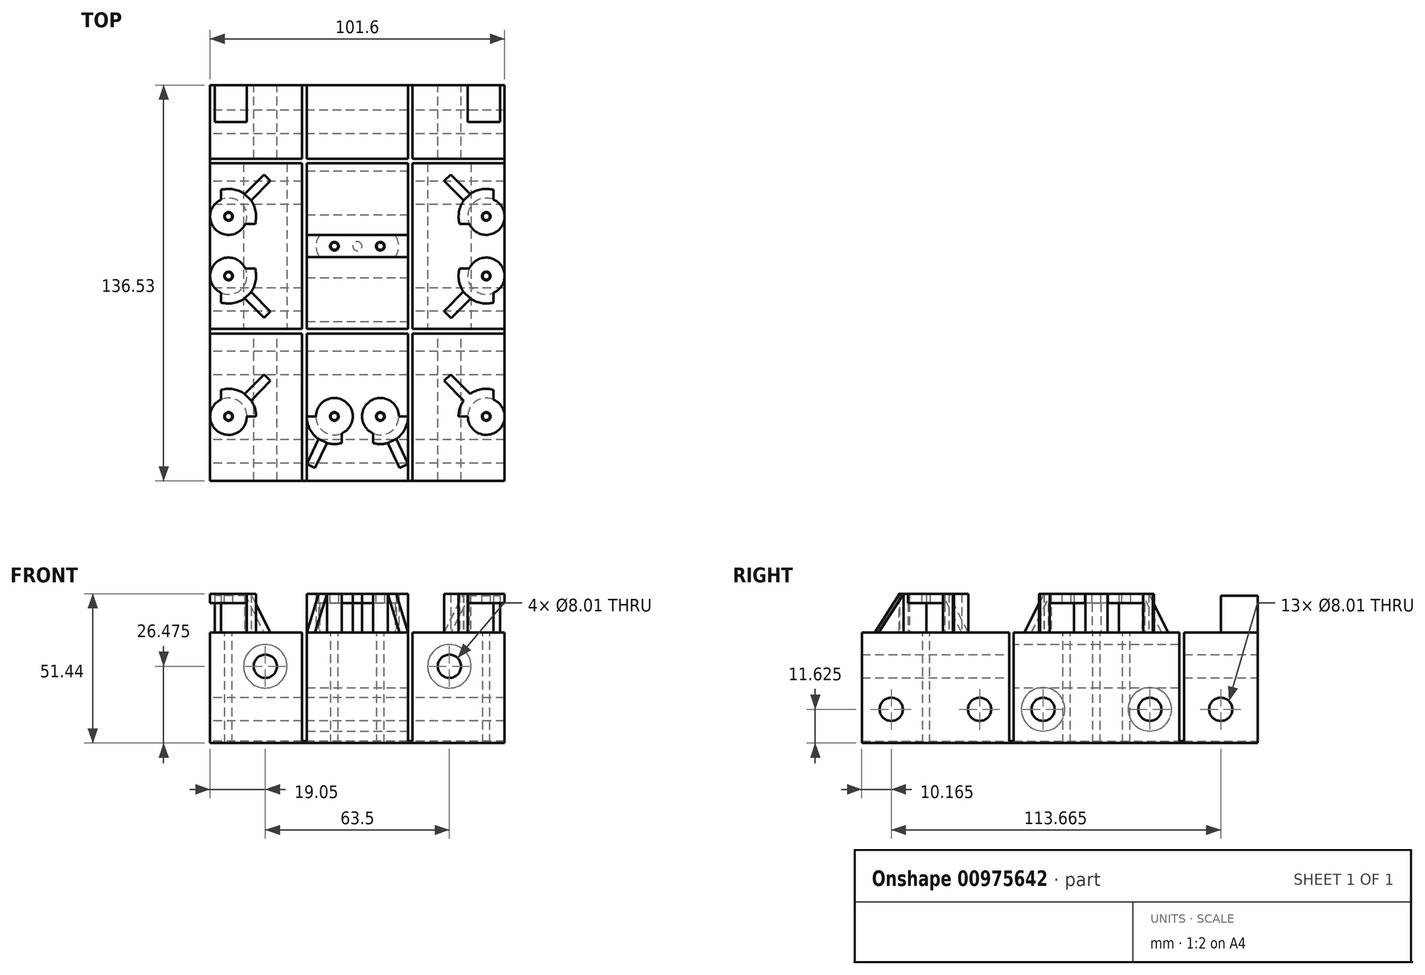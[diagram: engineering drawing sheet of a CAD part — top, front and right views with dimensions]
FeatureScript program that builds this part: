
annotation { "Feature Type Name" : "Feature", "Feature Type Description" : "" }
export const myFeature = defineFeature(function(context is Context, id is Id, definition is map)
    precondition{}
    {
        {
            var Q0;
            Q0=qCreatedBy(makeId("Front.planeOp"),FACE);
            var sketch = newSketch(context, id + "F0", { "sketchPlane" : qUnion([Q0])});
            skLineSegment(sketch, "E0.bottom", {"start": v(-50.8, 0) * mm, "end": v(50.8, 0) * mm});
            skLineSegment(sketch, "E0.top", {"start": v(-50.8, 38.1) * mm, "end": v(-19.05, 38.1) * mm});
            skLineSegment(sketch, "E0.left", {"start": v(-50.8, 0) * mm, "end": v(-50.8, 38.1) * mm});
            skLineSegment(sketch, "E0.right", {"start": v(50.8, 0) * mm, "end": v(50.8, 38.1) * mm});
            skLineSegment(sketch, "E1", {"start": v(-19.05, 38.1) * mm, "end": v(-19.05, 0.64) * mm});
            skLineSegment(sketch, "E2", {"start": v(-19.05, 0.64) * mm, "end": v(-17.46, 0.64) * mm});
            skLineSegment(sketch, "E3", {"start": v(-17.46, 0.64) * mm, "end": v(-17.46, 38.1) * mm});
            skLineSegment(sketch, "E4", {"start": v(17.46, 38.1) * mm, "end": v(17.46, 0.64) * mm});
            skLineSegment(sketch, "E5", {"start": v(17.46, 0.64) * mm, "end": v(19.05, 0.64) * mm});
            skLineSegment(sketch, "E6", {"start": v(19.05, 0.64) * mm, "end": v(19.05, 38.1) * mm});
            skLineSegment(sketch, "E7.trimOffspring", {"start": v(-17.46, 38.1) * mm, "end": v(17.46, 38.1) * mm});
            skLineSegment(sketch, "E8.trimOffspring", {"start": v(19.05, 38.1) * mm, "end": v(50.8, 38.1) * mm});
            skLineSegment(sketch, "E9", {"start": v(-50.8, 26.47) * mm, "end": v(50.8, 26.48) * mm, "construction": true});
            skCircle(sketch, "E10", {"center": v(-31.75, 26.47) * mm, "radius": 4 * mm});
            skCircle(sketch, "E11", {"center": v(31.75, 26.48) * mm, "radius": 4 * mm});
            skLineSegment(sketch, "E12", {"start": v(31.75, 38.1) * mm, "end": v(31.75, 0) * mm, "construction": true});
            skLineSegment(sketch, "E13", {"start": v(-31.75, 38.1) * mm, "end": v(-31.75, 0) * mm, "construction": true});
            skSolve(sketch);
        }
        {
            var Q0;
            Q0 = qSketchRegion(id + "F0", true);
            extrude(context, id + "F1", {"entities" : qUnion([Q0]), "depth" : 136.53 * mm, "offsetDistance" : 25.4 * mm});
        }
        {
            var Q0;
            Q0=makeQuery(id+"F1.opExtrude","SWEPT_FACE",FACE,{"disambiguationData":[OSD([sQuery(id+"F0.wireOp",EDGE,"E0.left")])]});
            var sketch = newSketch(context, id + "F2", { "sketchPlane" : qUnion([Q0])});
            skLineSegment(sketch, "E14.bottom", {"start": v(25.4, 64.27) * mm, "end": v(26.99, 64.27) * mm});
            skLineSegment(sketch, "E14.top", {"start": v(25.4, 0.64) * mm, "end": v(26.99, 0.64) * mm});
            skLineSegment(sketch, "E14.left", {"start": v(25.4, 64.27) * mm, "end": v(25.4, 0.64) * mm});
            skLineSegment(sketch, "E14.right", {"start": v(26.99, 64.27) * mm, "end": v(26.99, 0.64) * mm});
            skLineSegment(sketch, "E15.bottom", {"start": v(84.14, 64.27) * mm, "end": v(85.72, 64.27) * mm});
            skLineSegment(sketch, "E15.top", {"start": v(84.14, 0.64) * mm, "end": v(85.72, 0.64) * mm});
            skLineSegment(sketch, "E15.left", {"start": v(84.14, 64.27) * mm, "end": v(84.14, 0.64) * mm});
            skLineSegment(sketch, "E15.right", {"start": v(85.72, 64.27) * mm, "end": v(85.72, 0.64) * mm});
            skCircle(sketch, "E16", {"center": v(12.7, 11.63) * mm, "radius": 4 * mm});
            skCircle(sketch, "E17", {"center": v(37.15, 11.63) * mm, "radius": 4 * mm});
            skCircle(sketch, "E18", {"center": v(73.98, 11.63) * mm, "radius": 4 * mm});
            skCircle(sketch, "E19", {"center": v(95.88, 11.63) * mm, "radius": 4 * mm});
            skCircle(sketch, "E20", {"center": v(126.37, 11.63) * mm, "radius": 4 * mm});
            skLineSegment(sketch, "E21", {"start": v(0, 11.62) * mm, "end": v(175.3, 11.63) * mm, "construction": true});
            skSolve(sketch);
        }
        {
            var Q0;
            Q0 = qSketchRegion(id + "F2", true);
            extrude(context, id + "F3", {"entities" : qUnion([Q0]), "operationType" : NewBodyOperationType.REMOVE, "endBound" : BoundingType.THROUGH_ALL, "oppositeDirection" : true, "depth" : 25.4 * mm, "offsetDistance" : 25.4 * mm});
        }
        {
            var Q0;
            Q0=makeQuery(id+"F3.boolean.opBoolean","COPY",FACE,{"disambiguationData":[TD([makeQuery(id+"F1.opExtrude","SWEPT_FACE",FACE,{"disambiguationData":[OSD([sQuery(id+"F0.wireOp",EDGE,"E0.right")])]})])],"derivedFrom":makeQuery(id+"F3.opExtrude","SWEPT_FACE",FACE,{"disambiguationData":[OSD([sQuery(id+"F2.wireOp",EDGE,"E15.left")])]})});
            var sketch = newSketch(context, id + "F4", { "sketchPlane" : qUnion([Q0])});
            skCircle(sketch, "E22", {"center": v(31.75, 26.48) * mm, "radius": 7.5 * mm});
            skCircle(sketch, "E23.0", {"center": v(-31.75, 26.47) * mm, "radius": 4 * mm, "construction": true});
            skCircle(sketch, "E24", {"center": v(-31.75, 26.47) * mm, "radius": 7.5 * mm});
            skSolve(sketch);
        }
        {
            var Q0;
            Q0 = qSketchRegion(id + "F4", true);
            var Q1;
            Q1=makeQuery(id+"F3.boolean.opBoolean","COPY",FACE,{"disambiguationData":[TD([makeQuery(id+"F1.opExtrude","SWEPT_FACE",FACE,{"disambiguationData":[OSD([sQuery(id+"F0.wireOp",EDGE,"E0.right")])]})])],"derivedFrom":makeQuery(id+"F3.opExtrude","SWEPT_FACE",FACE,{"disambiguationData":[OSD([sQuery(id+"F2.wireOp",EDGE,"E14.left")])]})});
            extrude(context, id + "F5", {"entities" : qUnion([Q0]), "operationType" : NewBodyOperationType.REMOVE, "endBound" : BoundingType.UP_TO_SURFACE, "oppositeDirection" : true, "depth" : 25.4 * mm, "endBoundEntityFace" : qUnion([Q1]), "offsetDistance" : 25.4 * mm});
        }
        {
            var Q0;
            Q0=makeQuery(id+"F3.boolean.opBoolean","SPLIT",FACE,{"disambiguationData":[TD([makeQuery(id+"F3.opExtrude","SWEPT_FACE",FACE,{"disambiguationData":[OSD([sQuery(id+"F2.wireOp",EDGE,"E14.right")])]})])],"derivedFrom":makeQuery(id+"F1.opExtrude","SWEPT_FACE",FACE,{"disambiguationData":[OSD([sQuery(id+"F0.wireOp",EDGE,"E4")])]})});
            var sketch = newSketch(context, id + "F6", { "sketchPlane" : qUnion([Q0])});
            skCircle(sketch, "E25", {"center": v(-73.98, 11.63) * mm, "radius": 7.5 * mm});
            skCircle(sketch, "E26", {"center": v(-37.15, 11.63) * mm, "radius": 7.5 * mm});
            skSolve(sketch);
        }
        {
            var Q0;
            Q0 = qSketchRegion(id + "F6", true);
            var Q1;
            Q1=makeQuery(id+"F3.boolean.opBoolean","SPLIT",FACE,{"disambiguationData":[TD([makeQuery(id+"F3.opExtrude","SWEPT_FACE",FACE,{"disambiguationData":[OSD([sQuery(id+"F2.wireOp",EDGE,"E14.right")])]})])],"derivedFrom":makeQuery(id+"F1.opExtrude","SWEPT_FACE",FACE,{"disambiguationData":[OSD([sQuery(id+"F0.wireOp",EDGE,"E1")])]})});
            extrude(context, id + "F7", {"entities" : qUnion([Q0]), "operationType" : NewBodyOperationType.REMOVE, "endBound" : BoundingType.UP_TO_SURFACE, "oppositeDirection" : true, "depth" : 25.4 * mm, "endBoundEntityFace" : qUnion([Q1]), "offsetDistance" : 25.4 * mm});
        }
        {
            var Q0;
            {var subQ0=sQuery(id+"F0.wireOp",EDGE,"E8.trimOffspring");Q0=makeQuery(id+"F3.boolean.opBoolean","SPLIT",FACE,{"disambiguationData":[TD([makeQuery(id+"F3.opExtrude","SWEPT_FACE",FACE,{"disambiguationData":[OSD([sQuery(id+"F2.wireOp",EDGE,"E15.right")])]})])],"derivedFrom":makeQuery(id+"F1.opExtrude","SWEPT_FACE",FACE,{"disambiguationData":[OSD([subQ0])]})});}
            var sketch = newSketch(context, id + "F8", { "sketchPlane" : qUnion([Q0])});
            skLineSegment(sketch, "E27.0.0", {"start": v(19.05, -84.14) * mm, "end": v(50.8, -84.14) * mm, "construction": true});
            skLineSegment(sketch, "E27.0.1", {"start": v(50.8, -84.14) * mm, "end": v(50.8, -26.99) * mm, "construction": true});
            skLineSegment(sketch, "E27.0.2", {"start": v(50.8, -26.99) * mm, "end": v(19.05, -26.99) * mm, "construction": true});
            skLineSegment(sketch, "E27.0.3", {"start": v(19.05, -26.99) * mm, "end": v(19.05, -84.14) * mm, "construction": true});
            skLineSegment(sketch, "E28.0.0", {"start": v(17.46, -136.53) * mm, "end": v(17.46, -85.72) * mm, "construction": true});
            skLineSegment(sketch, "E28.0.1", {"start": v(17.46, -85.72) * mm, "end": v(-17.46, -85.72) * mm, "construction": true});
            skLineSegment(sketch, "E28.0.2", {"start": v(-17.46, -85.72) * mm, "end": v(-17.46, -136.53) * mm, "construction": true});
            skLineSegment(sketch, "E28.0.3", {"start": v(-17.46, -136.53) * mm, "end": v(17.46, -136.53) * mm, "construction": true});
            skLineSegment(sketch, "E29.0.0", {"start": v(-17.46, -84.14) * mm, "end": v(17.46, -84.14) * mm, "construction": true});
            skLineSegment(sketch, "E29.0.1", {"start": v(17.46, -84.14) * mm, "end": v(17.46, -26.99) * mm, "construction": true});
            skLineSegment(sketch, "E29.0.2", {"start": v(17.46, -26.99) * mm, "end": v(-17.46, -26.99) * mm, "construction": true});
            skLineSegment(sketch, "E29.0.3", {"start": v(-17.46, -26.99) * mm, "end": v(-17.46, -84.14) * mm, "construction": true});
            skLineSegment(sketch, "E30.0.0", {"start": v(-19.05, -136.53) * mm, "end": v(-19.05, -85.72) * mm, "construction": true});
            skLineSegment(sketch, "E30.0.1", {"start": v(-19.05, -85.72) * mm, "end": v(-50.8, -85.72) * mm, "construction": true});
            skLineSegment(sketch, "E30.0.2", {"start": v(-50.8, -85.72) * mm, "end": v(-50.8, -136.53) * mm, "construction": true});
            skLineSegment(sketch, "E30.0.3", {"start": v(-50.8, -136.53) * mm, "end": v(-19.05, -136.53) * mm, "construction": true});
            skLineSegment(sketch, "E31.0.0", {"start": v(-50.8, -84.14) * mm, "end": v(-19.05, -84.14) * mm, "construction": true});
            skLineSegment(sketch, "E31.0.1", {"start": v(-19.05, -84.14) * mm, "end": v(-19.05, -26.99) * mm, "construction": true});
            skLineSegment(sketch, "E31.0.2", {"start": v(-19.05, -26.99) * mm, "end": v(-50.8, -26.99) * mm, "construction": true});
            skLineSegment(sketch, "E31.0.3", {"start": v(-50.8, -26.99) * mm, "end": v(-50.8, -84.14) * mm, "construction": true});
            skLineSegment(sketch, "E32.0.0", {"start": v(-17.46, -25.4) * mm, "end": v(17.46, -25.4) * mm, "construction": true});
            skLineSegment(sketch, "E32.0.1", {"start": v(17.46, -25.4) * mm, "end": v(17.46, 0) * mm, "construction": true});
            skLineSegment(sketch, "E32.0.2", {"start": v(17.46, 0) * mm, "end": v(-17.46, 0) * mm, "construction": true});
            skLineSegment(sketch, "E32.0.3", {"start": v(-17.46, 0) * mm, "end": v(-17.46, -25.4) * mm, "construction": true});
            skLineSegment(sketch, "E33.0.0", {"start": v(19.05, -25.4) * mm, "end": v(50.8, -25.4) * mm, "construction": true});
            skLineSegment(sketch, "E33.0.1", {"start": v(50.8, -25.4) * mm, "end": v(50.8, 0) * mm, "construction": true});
            skLineSegment(sketch, "E33.0.2", {"start": v(50.8, 0) * mm, "end": v(19.05, 0) * mm, "construction": true});
            skLineSegment(sketch, "E33.0.3", {"start": v(19.05, 0) * mm, "end": v(19.05, -25.4) * mm, "construction": true});
            skLineSegment(sketch, "E34.0.0", {"start": v(-50.8, -25.4) * mm, "end": v(-19.05, -25.4) * mm, "construction": true});
            skLineSegment(sketch, "E34.0.1", {"start": v(-19.05, -25.4) * mm, "end": v(-19.05, 0) * mm, "construction": true});
            skLineSegment(sketch, "E34.0.2", {"start": v(-19.05, 0) * mm, "end": v(-50.8, 0) * mm, "construction": true});
            skLineSegment(sketch, "E34.0.3", {"start": v(-50.8, 0) * mm, "end": v(-50.8, -25.4) * mm, "construction": true});
            skLineSegment(sketch, "E35.0", {"start": v(50.8, -85.72) * mm, "end": v(19.05, -85.72) * mm, "construction": true});
            skLineSegment(sketch, "E36.0", {"start": v(19.05, -136.53) * mm, "end": v(19.05, -85.72) * mm, "construction": true});
            skLineSegment(sketch, "E37.0", {"start": v(19.05, -136.53) * mm, "end": v(50.8, -136.53) * mm, "construction": true});
            skLineSegment(sketch, "E38.0", {"start": v(50.8, -136.53) * mm, "end": v(50.8, -85.72) * mm, "construction": true});
            skLineSegment(sketch, "E39", {"start": v(44.45, 0) * mm, "end": v(44.45, -136.53) * mm, "construction": true});
            skPoint(sketch, "E40.endSnap0", {"position": v(0, -84.14) * mm});
            skLineSegment(sketch, "E41", {"start": v(-44.45, 0) * mm, "end": v(-44.45, -136.53) * mm, "construction": true});
            skLineSegment(sketch, "E42", {"start": v(-50.8, -114.3) * mm, "end": v(50.8, -114.3) * mm, "construction": true});
            skLineSegment(sketch, "E43", {"start": v(-50.8, -55.56) * mm, "end": v(50.8, -55.56) * mm, "construction": true});
            skLineSegment(sketch, "E44", {"start": v(50.8, -65.82) * mm, "end": v(-50.8, -65.82) * mm, "construction": true});
            skLineSegment(sketch, "E45", {"start": v(50.8, -45.3) * mm, "end": v(-50.8, -45.3) * mm, "construction": true});
            skCircle(sketch, "E46", {"center": v(7.92, -55.56) * mm, "radius": 4.75 * mm, "construction": true});
            skCircle(sketch, "E47", {"center": v(44.45, -45.3) * mm, "radius": 4.75 * mm, "construction": true});
            skCircle(sketch, "E48", {"center": v(44.45, -65.82) * mm, "radius": 4.75 * mm, "construction": true});
            skCircle(sketch, "E49", {"center": v(-44.45, -45.3) * mm, "radius": 4.75 * mm, "construction": true});
            skCircle(sketch, "E50", {"center": v(-44.45, -65.82) * mm, "radius": 4.75 * mm, "construction": true});
            skCircle(sketch, "E51", {"center": v(44.45, -114.3) * mm, "radius": 4.75 * mm, "construction": true});
            skCircle(sketch, "E52", {"center": v(-44.45, -114.3) * mm, "radius": 4.75 * mm, "construction": true});
            skCircle(sketch, "E53", {"center": v(0, -55.56) * mm, "radius": 3.18 * mm, "construction": true});
            skLineSegment(sketch, "E54", {"start": v(-50.8, -61.07) * mm, "end": v(50.8, -61.07) * mm, "construction": true});
            skLineSegment(sketch, "E55", {"start": v(50.8, -50.05) * mm, "end": v(-50.8, -50.05) * mm, "construction": true});
            skLineSegment(sketch, "E56", {"start": v(-50.8, -60.31) * mm, "end": v(50.8, -60.31) * mm, "construction": true});
            skLineSegment(sketch, "E57", {"start": v(-50.8, -50.81) * mm, "end": v(50.8, -50.81) * mm, "construction": true});
            skCircle(sketch, "E58", {"center": v(-7.92, -55.56) * mm, "radius": 4.75 * mm, "construction": true});
            skCircle(sketch, "E59", {"center": v(-44.45, -45.3) * mm, "radius": 1.25 * mm});
            skCircle(sketch, "E60", {"center": v(44.45, -45.3) * mm, "radius": 1.25 * mm});
            skCircle(sketch, "E61", {"center": v(7.92, -55.56) * mm, "radius": 1.25 * mm});
            skCircle(sketch, "E62", {"center": v(-7.92, -55.56) * mm, "radius": 1.25 * mm});
            skCircle(sketch, "E63", {"center": v(-44.45, -65.82) * mm, "radius": 1.25 * mm});
            skCircle(sketch, "E64", {"center": v(-44.45, -114.3) * mm, "radius": 1.25 * mm});
            skCircle(sketch, "E65", {"center": v(44.45, -65.82) * mm, "radius": 1.25 * mm});
            skCircle(sketch, "E66", {"center": v(44.45, -114.3) * mm, "radius": 1.25 * mm});
            skCircle(sketch, "E67", {"center": v(7.94, -114.3) * mm, "radius": 1.25 * mm});
            skCircle(sketch, "E68", {"center": v(-7.94, -114.3) * mm, "radius": 1.25 * mm});
            skCircle(sketch, "E69", {"center": v(7.94, -114.3) * mm, "radius": 4.75 * mm, "construction": true});
            skCircle(sketch, "E70", {"center": v(-7.94, -114.3) * mm, "radius": 4.75 * mm, "construction": true});
            skSolve(sketch);
        }
        {
            var Q0;
            Q0 = qSketchRegion(id + "F8", true);
            extrude(context, id + "F9", {"entities" : qUnion([Q0]), "operationType" : NewBodyOperationType.REMOVE, "endBound" : BoundingType.THROUGH_ALL, "oppositeDirection" : true, "depth" : 25.4 * mm, "offsetDistance" : 25.4 * mm});
        }
        {
            var Q0;
            {var subQ0=sQuery(id+"F0.wireOp",EDGE,"E8.trimOffspring");Q0=makeQuery(id+"F3.boolean.opBoolean","SPLIT",FACE,{"disambiguationData":[TD([makeQuery(id+"F3.opExtrude","SWEPT_FACE",FACE,{"disambiguationData":[OSD([sQuery(id+"F2.wireOp",EDGE,"E14.left")])]})])],"derivedFrom":makeQuery(id+"F1.opExtrude","SWEPT_FACE",FACE,{"disambiguationData":[OSD([subQ0])]})});}
            var sketch = newSketch(context, id + "F10", { "sketchPlane" : qUnion([Q0])});
            skCircle(sketch, "E71.0", {"center": v(44.45, -45.3) * mm, "radius": 4.75 * mm, "construction": true});
            skCircle(sketch, "E72.0", {"center": v(-44.45, -45.3) * mm, "radius": 4.75 * mm, "construction": true});
            skLineSegment(sketch, "E73.bottom", {"start": v(49.2, -12.7) * mm, "end": v(38.1, -12.7) * mm});
            skLineSegment(sketch, "E73.top", {"start": v(49.2, 0) * mm, "end": v(38.1, 0) * mm});
            skLineSegment(sketch, "E73.left", {"start": v(49.2, -12.7) * mm, "end": v(49.2, 0) * mm});
            skLineSegment(sketch, "E73.right", {"start": v(38.1, -12.7) * mm, "end": v(38.1, 0) * mm});
            skLineSegment(sketch, "E74.bottom", {"start": v(-38.1, 0) * mm, "end": v(-49.2, 0) * mm});
            skLineSegment(sketch, "E74.top", {"start": v(-38.1, -12.7) * mm, "end": v(-49.2, -12.7) * mm});
            skLineSegment(sketch, "E74.left", {"start": v(-38.1, 0) * mm, "end": v(-38.1, -12.7) * mm});
            skLineSegment(sketch, "E74.right", {"start": v(-49.2, 0) * mm, "end": v(-49.2, -12.7) * mm});
            skSolve(sketch);
        }
        {
            var Q0;
            Q0 = qSketchRegion(id + "F10", true);
            extrude(context, id + "F11", {"entities" : qUnion([Q0]), "operationType" : NewBodyOperationType.ADD, "depth" : 12.7 * mm, "offsetDistance" : 25.4 * mm});
        }
        {
            var Q0;
            {var subQ2=sQuery(id+"F0.wireOp",EDGE,"E0.top");Q0=makeQuery(id+"F3.boolean.opBoolean","SPLIT",FACE,{"disambiguationData":[TD([makeQuery(id+"F3.opExtrude","SWEPT_FACE",FACE,{"disambiguationData":[OSD([sQuery(id+"F2.wireOp",EDGE,"E15.right")])]})])],"derivedFrom":makeQuery(id+"F1.opExtrude","SWEPT_FACE",FACE,{"disambiguationData":[OSD([subQ2])]})});}
            var sketch = newSketch(context, id + "F12", { "sketchPlane" : qUnion([Q0])});
            skCircle(sketch, "E75.0", {"center": v(-44.45, -114.3) * mm, "radius": 4.75 * mm, "construction": true});
            skCircle(sketch, "E76.0", {"center": v(-7.94, -114.3) * mm, "radius": 4.75 * mm, "construction": true});
            skCircle(sketch, "E77.0", {"center": v(7.94, -114.3) * mm, "radius": 4.75 * mm, "construction": true});
            skCircle(sketch, "E78.0", {"center": v(-44.45, -65.82) * mm, "radius": 4.75 * mm, "construction": true});
            skCircle(sketch, "E79.0", {"center": v(44.45, -114.3) * mm, "radius": 4.75 * mm, "construction": true});
            skCircle(sketch, "E80.0", {"center": v(44.45, -65.82) * mm, "radius": 4.75 * mm, "construction": true});
            skCircle(sketch, "E81.0", {"center": v(44.45, -45.3) * mm, "radius": 4.75 * mm, "construction": true});
            skCircle(sketch, "E82.0", {"center": v(7.92, -55.56) * mm, "radius": 4.75 * mm, "construction": true});
            skCircle(sketch, "E83.0", {"center": v(-7.92, -55.56) * mm, "radius": 4.75 * mm, "construction": true});
            skCircle(sketch, "E84.0", {"center": v(-44.45, -45.3) * mm, "radius": 4.75 * mm, "construction": true});
            skArc(sketch, "E85", {"start": v(-38.1, -114.3) * mm, "mid": v(-40.97, -108.99) * mm, "end": v(-47, -108.48) * mm});
            skArc(sketch, "E86", {"start": v(-34.93, -114.3) * mm, "mid": v(-38.68, -106.72) * mm, "end": v(-47, -105.12) * mm});
            skLineSegment(sketch, "E87", {"start": v(38.1, -114.3) * mm, "end": v(34.92, -114.3) * mm});
            skLineSegment(sketch, "E88", {"start": v(-47, -36.12) * mm, "end": v(-47, -39.48) * mm});
            skArc(sketch, "E89", {"start": v(-47, -71.64) * mm, "mid": v(-39.96, -70.31) * mm, "end": v(-38.63, -63.28) * mm});
            skArc(sketch, "E90", {"start": v(-38.63, -47.84) * mm, "mid": v(-39.96, -40.81) * mm, "end": v(-47, -39.48) * mm});
            skArc(sketch, "E91", {"start": v(-35.27, -47.84) * mm, "mid": v(-37.71, -38.57) * mm, "end": v(-47, -36.12) * mm});
            skArc(sketch, "E92", {"start": v(-47, -75) * mm, "mid": v(-37.71, -72.56) * mm, "end": v(-35.27, -63.28) * mm});
            skArc(sketch, "E93", {"start": v(38.63, -63.28) * mm, "mid": v(39.96, -70.31) * mm, "end": v(46.99, -71.64) * mm});
            skArc(sketch, "E94", {"start": v(35.27, -63.28) * mm, "mid": v(37.71, -72.56) * mm, "end": v(47, -75) * mm});
            skArc(sketch, "E95", {"start": v(46.99, -39.48) * mm, "mid": v(39.96, -40.81) * mm, "end": v(38.63, -47.84) * mm});
            skArc(sketch, "E96", {"start": v(46.99, -36.12) * mm, "mid": v(37.71, -38.57) * mm, "end": v(35.27, -47.84) * mm});
            skArc(sketch, "E97", {"start": v(46.99, -108.48) * mm, "mid": v(40.97, -108.99) * mm, "end": v(38.1, -114.3) * mm});
            skArc(sketch, "E98", {"start": v(46.99, -105.12) * mm, "mid": v(38.68, -106.72) * mm, "end": v(34.92, -114.3) * mm});
            skLineSegment(sketch, "E99", {"start": v(46.99, -108.48) * mm, "end": v(46.99, -105.12) * mm});
            skLineSegment(sketch, "E100", {"start": v(38.63, -47.84) * mm, "end": v(35.27, -47.84) * mm});
            skLineSegment(sketch, "E101", {"start": v(38.63, -63.28) * mm, "end": v(35.27, -63.28) * mm});
            skLineSegment(sketch, "E102.trimOffspring", {"start": v(46.99, -39.48) * mm, "end": v(46.99, -36.12) * mm});
            skLineSegment(sketch, "E103.trimOffspring", {"start": v(46.99, -75) * mm, "end": v(46.99, -71.64) * mm});
            skLineSegment(sketch, "E104.trimOffspring", {"start": v(-47, -71.64) * mm, "end": v(-47, -75) * mm});
            skLineSegment(sketch, "E105.trimOffspring", {"start": v(-47, -105.12) * mm, "end": v(-47, -108.48) * mm});
            skLineSegment(sketch, "E106.trimOffspring", {"start": v(-35.27, -47.84) * mm, "end": v(-38.63, -47.84) * mm});
            skLineSegment(sketch, "E107.trimOffspring", {"start": v(-35.27, -63.28) * mm, "end": v(-38.63, -63.28) * mm});
            skArc(sketch, "E108", {"start": v(-14.29, -114.3) * mm, "mid": v(-11.42, -119.61) * mm, "end": v(-5.4, -120.12) * mm});
            skArc(sketch, "E109", {"start": v(-17.46, -114.3) * mm, "mid": v(-13.7, -121.88) * mm, "end": v(-5.4, -123.48) * mm});
            skArc(sketch, "E110", {"start": v(5.4, -120.12) * mm, "mid": v(11.42, -119.61) * mm, "end": v(14.29, -114.3) * mm});
            skLineSegment(sketch, "E111", {"start": v(-5.4, -123.48) * mm, "end": v(-5.4, -120.12) * mm});
            skLineSegment(sketch, "E112", {"start": v(5.4, -123.48) * mm, "end": v(5.4, -120.12) * mm});
            skArc(sketch, "E113.trimOffspring", {"start": v(5.4, -123.48) * mm, "mid": v(13.7, -121.88) * mm, "end": v(17.46, -114.3) * mm});
            skLineSegment(sketch, "E114.trimOffspring", {"start": v(-14.29, -114.3) * mm, "end": v(-17.46, -114.3) * mm});
            skLineSegment(sketch, "E115.trimOffspring", {"start": v(-34.93, -114.3) * mm, "end": v(-38.1, -114.3) * mm});
            skLineSegment(sketch, "E116.trimOffspring", {"start": v(17.46, -114.3) * mm, "end": v(14.29, -114.3) * mm});
            skArc(sketch, "E117", {"start": v(-13, -51.75) * mm, "mid": v(-14.27, -55.56) * mm, "end": v(-13, -59.37) * mm});
            skArc(sketch, "E118", {"start": v(13, -59.37) * mm, "mid": v(14.27, -55.56) * mm, "end": v(13, -51.75) * mm});
            skLineSegment(sketch, "E119", {"start": v(-17.46, -51.75) * mm, "end": v(-13, -51.75) * mm});
            skLineSegment(sketch, "E120", {"start": v(17.46, -51.75) * mm, "end": v(17.46, -59.37) * mm});
            skLineSegment(sketch, "E121", {"start": v(17.46, -59.37) * mm, "end": v(13, -59.37) * mm});
            skLineSegment(sketch, "E122", {"start": v(-17.46, -59.37) * mm, "end": v(-17.46, -51.75) * mm});
            skLineSegment(sketch, "E123.0.1", {"start": v(-17.46, -84.14) * mm, "end": v(-17.46, -26.99) * mm, "construction": true});
            skLineSegment(sketch, "E123.0.3", {"start": v(-17.46, -26.99) * mm, "end": v(-17.46, -84.14) * mm, "construction": true});
            skLineSegment(sketch, "E124.0", {"start": v(17.46, -84.14) * mm, "end": v(17.46, -26.99) * mm, "construction": true});
            skLineSegment(sketch, "E125", {"start": v(-7.92, -55.56) * mm, "end": v(7.92, -55.56) * mm, "construction": true});
            skCircle(sketch, "E126", {"center": v(0, -55.56) * mm, "radius": 1.57 * mm});
            skLineSegment(sketch, "E127.trimOffspring", {"start": v(-13, -59.37) * mm, "end": v(-17.46, -59.37) * mm});
            skLineSegment(sketch, "E128.trimOffspring", {"start": v(13, -51.75) * mm, "end": v(17.46, -51.75) * mm});
            skSolve(sketch);
        }
        {
            var Q0;
            Q0 = qSketchRegion(id + "F12", true);
            extrude(context, id + "F13", {"entities" : qUnion([Q0]), "operationType" : NewBodyOperationType.ADD, "depth" : 10.16 * mm, "offsetDistance" : 25.4 * mm});
        }
        {
            var Q0;
            Q0=makeQuery(id+"F13.opExtrude","CAP_FACE",FACE,{"disambiguationData":[OSD([sQuery(id+"F12.wireOp",EDGE,"E87"),sQuery(id+"F12.wireOp",EDGE,"E97"),sQuery(id+"F12.wireOp",EDGE,"E98"),sQuery(id+"F12.wireOp",EDGE,"E99")])],"isStart":false});
            var sketch = newSketch(context, id + "F14", { "sketchPlane" : qUnion([Q0])});
            skCircle(sketch, "E129.0", {"center": v(44.45, -114.3) * mm, "radius": 4.75 * mm, "construction": true});
            skLineSegment(sketch, "E130.0", {"start": v(46.99, -108.48) * mm, "end": v(46.99, -105.12) * mm});
            skArc(sketch, "E131.0", {"start": v(46.99, -105.12) * mm, "mid": v(38.68, -106.72) * mm, "end": v(34.92, -114.3) * mm});
            skLineSegment(sketch, "E132.0", {"start": v(38.1, -114.3) * mm, "end": v(34.92, -114.3) * mm});
            skArc(sketch, "E133", {"start": v(38.1, -114.3) * mm, "mid": v(47.93, -119.61) * mm, "end": v(46.99, -108.48) * mm});
            skLineSegment(sketch, "E134.0", {"start": v(17.46, -114.3) * mm, "end": v(14.29, -114.3) * mm});
            skArc(sketch, "E135.0", {"start": v(5.4, -123.48) * mm, "mid": v(13.7, -121.88) * mm, "end": v(17.46, -114.3) * mm});
            skLineSegment(sketch, "E136.0", {"start": v(5.4, -123.48) * mm, "end": v(5.4, -120.12) * mm});
            skLineSegment(sketch, "E137.0", {"start": v(-5.4, -123.48) * mm, "end": v(-5.4, -120.12) * mm});
            skLineSegment(sketch, "E138.0", {"start": v(-14.29, -114.3) * mm, "end": v(-17.46, -114.3) * mm});
            skArc(sketch, "E139.0", {"start": v(-17.46, -114.3) * mm, "mid": v(-13.7, -121.88) * mm, "end": v(-5.4, -123.48) * mm});
            skCircle(sketch, "E140.0", {"center": v(-7.94, -114.3) * mm, "radius": 4.75 * mm, "construction": true});
            skCircle(sketch, "E141.0", {"center": v(7.94, -114.3) * mm, "radius": 4.75 * mm, "construction": true});
            skArc(sketch, "E142", {"start": v(-5.4, -120.12) * mm, "mid": v(-4.46, -108.99) * mm, "end": v(-14.29, -114.3) * mm});
            skArc(sketch, "E143", {"start": v(14.29, -114.3) * mm, "mid": v(4.46, -108.99) * mm, "end": v(5.4, -120.12) * mm});
            skArc(sketch, "E144.0", {"start": v(-34.93, -114.3) * mm, "mid": v(-38.68, -106.72) * mm, "end": v(-47, -105.12) * mm});
            skLineSegment(sketch, "E145.0", {"start": v(-47, -105.12) * mm, "end": v(-47, -108.48) * mm});
            skLineSegment(sketch, "E146.0", {"start": v(-34.93, -114.3) * mm, "end": v(-38.1, -114.3) * mm});
            skCircle(sketch, "E147.0", {"center": v(-44.45, -114.3) * mm, "radius": 4.75 * mm, "construction": true});
            skArc(sketch, "E148", {"start": v(-47, -108.48) * mm, "mid": v(-47.93, -119.61) * mm, "end": v(-38.1, -114.3) * mm});
            skCircle(sketch, "E149.0", {"center": v(-44.45, -45.3) * mm, "radius": 4.75 * mm, "construction": true});
            skCircle(sketch, "E150.0", {"center": v(-44.45, -65.82) * mm, "radius": 4.75 * mm, "construction": true});
            skLineSegment(sketch, "E151.0", {"start": v(-35.27, -47.84) * mm, "end": v(-38.63, -47.84) * mm});
            skArc(sketch, "E151.1", {"start": v(-35.27, -47.84) * mm, "mid": v(-37.71, -38.57) * mm, "end": v(-47, -36.12) * mm});
            skLineSegment(sketch, "E152.0", {"start": v(-47, -36.12) * mm, "end": v(-47, -39.48) * mm});
            skArc(sketch, "E153.0", {"start": v(-47, -75) * mm, "mid": v(-37.71, -72.56) * mm, "end": v(-35.27, -63.28) * mm});
            skLineSegment(sketch, "E154.0", {"start": v(-35.27, -63.28) * mm, "end": v(-38.63, -63.28) * mm});
            skLineSegment(sketch, "E155.0", {"start": v(-47, -71.64) * mm, "end": v(-47, -75) * mm});
            skArc(sketch, "E156", {"start": v(-38.63, -63.28) * mm, "mid": v(-48.94, -61.33) * mm, "end": v(-47, -71.64) * mm});
            skArc(sketch, "E157", {"start": v(-47, -39.48) * mm, "mid": v(-48.94, -49.8) * mm, "end": v(-38.63, -47.84) * mm});
            skLineSegment(sketch, "E158.0", {"start": v(17.46, -51.75) * mm, "end": v(17.46, -59.37) * mm});
            skLineSegment(sketch, "E159.0", {"start": v(-17.46, -59.37) * mm, "end": v(-17.46, -51.75) * mm});
            skCircle(sketch, "E160.0", {"center": v(44.45, -45.3) * mm, "radius": 4.75 * mm, "construction": true});
            skCircle(sketch, "E161.0", {"center": v(44.45, -65.82) * mm, "radius": 4.75 * mm, "construction": true});
            skLineSegment(sketch, "E162.0", {"start": v(46.99, -39.48) * mm, "end": v(46.99, -36.12) * mm});
            skLineSegment(sketch, "E163.0", {"start": v(46.99, -75) * mm, "end": v(46.99, -71.64) * mm});
            skArc(sketch, "E163.1", {"start": v(35.27, -63.28) * mm, "mid": v(37.71, -72.56) * mm, "end": v(47, -75) * mm});
            skLineSegment(sketch, "E163.2", {"start": v(38.63, -47.84) * mm, "end": v(35.27, -47.84) * mm});
            skLineSegment(sketch, "E163.3", {"start": v(38.63, -63.28) * mm, "end": v(35.27, -63.28) * mm});
            skArc(sketch, "E163.4", {"start": v(46.99, -36.12) * mm, "mid": v(37.71, -38.57) * mm, "end": v(35.27, -47.84) * mm});
            skArc(sketch, "E164", {"start": v(38.63, -47.84) * mm, "mid": v(48.94, -49.8) * mm, "end": v(46.99, -39.48) * mm});
            skArc(sketch, "E165", {"start": v(46.99, -71.64) * mm, "mid": v(48.94, -61.33) * mm, "end": v(38.63, -63.28) * mm});
            skLineSegment(sketch, "E166", {"start": v(-17.46, -59.37) * mm, "end": v(17.46, -59.37) * mm});
            skLineSegment(sketch, "E167", {"start": v(-17.46, -51.75) * mm, "end": v(17.46, -51.75) * mm});
            skSolve(sketch);
        }
        {
            var Q0;
            Q0 = qSketchRegion(id + "F14", true);
            extrude(context, id + "F15", {"entities" : qUnion([Q0]), "operationType" : NewBodyOperationType.ADD, "depth" : 3.17 * mm, "offsetDistance" : 25.4 * mm});
        }
        {
            var Q0;
            Q0=makeQuery(id+"F15.opExtrude","CAP_FACE",FACE,{"disambiguationData":[OSD([sQuery(id+"F14.wireOp",EDGE,"E130.0"),sQuery(id+"F14.wireOp",EDGE,"E131.0"),sQuery(id+"F14.wireOp",EDGE,"E132.0"),sQuery(id+"F14.wireOp",EDGE,"E133")])],"isStart":false});
            var sketch = newSketch(context, id + "F16", { "sketchPlane" : qUnion([Q0])});
            skCircle(sketch, "E168", {"center": v(44.45, -114.3) * mm, "radius": 1.5 * mm});
            skArc(sketch, "E169.0", {"start": v(46.99, -71.64) * mm, "mid": v(48.94, -61.33) * mm, "end": v(38.63, -63.28) * mm, "construction": true});
            skCircle(sketch, "E170.0", {"center": v(44.45, -45.3) * mm, "radius": 4.75 * mm, "construction": true});
            skCircle(sketch, "E171.0", {"center": v(7.94, -114.3) * mm, "radius": 4.75 * mm, "construction": true});
            skCircle(sketch, "E172.0", {"center": v(-7.94, -114.3) * mm, "radius": 4.75 * mm, "construction": true});
            skCircle(sketch, "E173.0", {"center": v(-44.45, -114.3) * mm, "radius": 4.75 * mm, "construction": true});
            skCircle(sketch, "E174.0", {"center": v(-44.45, -65.82) * mm, "radius": 4.75 * mm, "construction": true});
            skCircle(sketch, "E175.0", {"center": v(-44.45, -45.3) * mm, "radius": 4.75 * mm, "construction": true});
            skCircle(sketch, "E176.0", {"center": v(-7.92, -55.56) * mm, "radius": 4.75 * mm, "construction": true});
            skCircle(sketch, "E177.0", {"center": v(7.92, -55.56) * mm, "radius": 4.75 * mm, "construction": true});
            skCircle(sketch, "E178", {"center": v(44.45, -45.3) * mm, "radius": 1.5 * mm});
            skCircle(sketch, "E179", {"center": v(44.45, -65.82) * mm, "radius": 1.5 * mm});
            skCircle(sketch, "E180", {"center": v(7.92, -55.56) * mm, "radius": 1.5 * mm});
            skCircle(sketch, "E181", {"center": v(-7.92, -55.56) * mm, "radius": 1.5 * mm});
            skCircle(sketch, "E182", {"center": v(-44.45, -45.3) * mm, "radius": 1.5 * mm});
            skCircle(sketch, "E183", {"center": v(-44.45, -65.82) * mm, "radius": 1.5 * mm});
            skCircle(sketch, "E184", {"center": v(-44.45, -114.3) * mm, "radius": 1.5 * mm});
            skCircle(sketch, "E185", {"center": v(-7.94, -114.3) * mm, "radius": 1.5 * mm});
            skCircle(sketch, "E186", {"center": v(7.94, -114.3) * mm, "radius": 1.5 * mm});
            skSolve(sketch);
        }
        {
            var Q0;
            Q0 = qSketchRegion(id + "F16", true);
            extrude(context, id + "F17", {"entities" : qUnion([Q0]), "operationType" : NewBodyOperationType.REMOVE, "endBound" : BoundingType.UP_TO_NEXT, "oppositeDirection" : true, "depth" : 25.4 * mm, "offsetDistance" : 25.4 * mm});
        }
        {
            var Q0;
            Q0=makeQuery(id+"F3.boolean.opBoolean","SPLIT",FACE,{"disambiguationData":[TD([makeQuery(id+"F3.opExtrude","SWEPT_FACE",FACE,{"disambiguationData":[OSD([sQuery(id+"F2.wireOp",EDGE,"E14.right")])]})])],"derivedFrom":makeQuery(id+"F1.opExtrude","SWEPT_FACE",FACE,{"disambiguationData":[OSD([sQuery(id+"F0.wireOp",EDGE,"E7.trimOffspring")])]})});
            var sketch = newSketch(context, id + "F18", { "sketchPlane" : qUnion([Q0])});
            skLineSegment(sketch, "E187.bottom", {"start": v(32.2, -30.8) * mm, "end": v(38.93, -37.54) * mm});
            skLineSegment(sketch, "E187.top", {"start": v(29.95, -33.05) * mm, "end": v(36.69, -39.78) * mm});
            skLineSegment(sketch, "E187.left", {"start": v(32.2, -30.8) * mm, "end": v(29.95, -33.05) * mm});
            skLineSegment(sketch, "E187.right", {"start": v(38.93, -37.54) * mm, "end": v(36.69, -39.78) * mm});
            skArc(sketch, "E188.0", {"start": v(46.99, -36.12) * mm, "mid": v(37.71, -38.57) * mm, "end": v(35.27, -47.84) * mm, "construction": true});
            skLineSegment(sketch, "E189", {"start": v(44.45, -45.3) * mm, "end": v(31.07, -31.92) * mm});
            skLineSegment(sketch, "E190.bottom", {"start": v(39.06, -73.68) * mm, "end": v(32.32, -80.41) * mm});
            skLineSegment(sketch, "E190.top", {"start": v(36.6, -71.21) * mm, "end": v(29.86, -77.95) * mm});
            skLineSegment(sketch, "E190.left", {"start": v(39.06, -73.68) * mm, "end": v(36.6, -71.21) * mm});
            skLineSegment(sketch, "E190.right", {"start": v(32.32, -80.41) * mm, "end": v(29.86, -77.95) * mm});
            skArc(sketch, "E191.0", {"start": v(35.27, -63.28) * mm, "mid": v(37.71, -72.56) * mm, "end": v(47, -75) * mm, "construction": true});
            skLineSegment(sketch, "E192", {"start": v(44.45, -65.82) * mm, "end": v(31.1, -79.18) * mm, "construction": true});
            skArc(sketch, "E193.0", {"start": v(-47, -75) * mm, "mid": v(-37.71, -72.56) * mm, "end": v(-35.27, -63.28) * mm, "construction": true});
            skLineSegment(sketch, "E194.bottom", {"start": v(-38.93, -73.59) * mm, "end": v(-32.2, -80.32) * mm});
            skLineSegment(sketch, "E194.top", {"start": v(-36.69, -71.34) * mm, "end": v(-29.95, -78.08) * mm});
            skLineSegment(sketch, "E194.left", {"start": v(-38.93, -73.59) * mm, "end": v(-36.69, -71.34) * mm});
            skLineSegment(sketch, "E194.right", {"start": v(-32.2, -80.32) * mm, "end": v(-29.95, -78.08) * mm});
            skLineSegment(sketch, "E195", {"start": v(-44.45, -65.82) * mm, "end": v(-31.07, -79.2) * mm, "construction": true});
            skArc(sketch, "E196.0", {"start": v(-35.27, -47.84) * mm, "mid": v(-37.71, -38.57) * mm, "end": v(-47, -36.12) * mm, "construction": true});
            skLineSegment(sketch, "E197.bottom", {"start": v(-38.93, -37.54) * mm, "end": v(-32.2, -30.8) * mm});
            skLineSegment(sketch, "E197.top", {"start": v(-36.69, -39.78) * mm, "end": v(-29.95, -33.05) * mm});
            skLineSegment(sketch, "E197.left", {"start": v(-38.93, -37.54) * mm, "end": v(-36.69, -39.78) * mm});
            skLineSegment(sketch, "E197.right", {"start": v(-32.2, -30.8) * mm, "end": v(-29.95, -33.05) * mm});
            skLineSegment(sketch, "E198", {"start": v(-44.45, -45.3) * mm, "end": v(-31.07, -31.92) * mm, "construction": true});
            skArc(sketch, "E199.0", {"start": v(-34.93, -114.3) * mm, "mid": v(-38.68, -106.72) * mm, "end": v(-47, -105.12) * mm, "construction": true});
            skLineSegment(sketch, "E200.bottom", {"start": v(-38.93, -106.54) * mm, "end": v(-32.2, -99.8) * mm});
            skLineSegment(sketch, "E200.top", {"start": v(-36.69, -108.78) * mm, "end": v(-29.95, -102.05) * mm});
            skLineSegment(sketch, "E200.left", {"start": v(-38.93, -106.54) * mm, "end": v(-36.69, -108.78) * mm});
            skLineSegment(sketch, "E200.right", {"start": v(-32.2, -99.8) * mm, "end": v(-29.95, -102.05) * mm});
            skLineSegment(sketch, "E201", {"start": v(-44.45, -114.3) * mm, "end": v(-31.07, -100.92) * mm, "construction": true});
            skArc(sketch, "E202.0", {"start": v(-17.46, -114.3) * mm, "mid": v(-13.7, -121.88) * mm, "end": v(-5.4, -123.48) * mm, "construction": true});
            skLineSegment(sketch, "E203.bottom", {"start": v(-14.6, -132.08) * mm, "end": v(-10.52, -123.47) * mm});
            skLineSegment(sketch, "E203.top", {"start": v(-17.46, -130.72) * mm, "end": v(-13.39, -122.11) * mm});
            skLineSegment(sketch, "E203.left", {"start": v(-14.6, -132.08) * mm, "end": v(-17.46, -130.72) * mm});
            skLineSegment(sketch, "E203.right", {"start": v(-10.52, -123.47) * mm, "end": v(-13.39, -122.11) * mm});
            skLineSegment(sketch, "E204", {"start": v(-16.03, -131.4) * mm, "end": v(-7.94, -114.3) * mm, "construction": true});
            skArc(sketch, "E205.0", {"start": v(5.4, -123.48) * mm, "mid": v(13.7, -121.88) * mm, "end": v(17.46, -114.3) * mm, "construction": true});
            skLineSegment(sketch, "E206.bottom", {"start": v(13.39, -122.11) * mm, "end": v(17.46, -130.72) * mm});
            skLineSegment(sketch, "E206.top", {"start": v(10.52, -123.47) * mm, "end": v(14.6, -132.08) * mm});
            skLineSegment(sketch, "E206.left", {"start": v(13.39, -122.11) * mm, "end": v(10.52, -123.47) * mm});
            skLineSegment(sketch, "E206.right", {"start": v(17.46, -130.72) * mm, "end": v(14.6, -132.08) * mm});
            skLineSegment(sketch, "E207", {"start": v(7.94, -114.3) * mm, "end": v(16.03, -131.4) * mm, "construction": true});
            skArc(sketch, "E208.0", {"start": v(46.99, -105.12) * mm, "mid": v(38.68, -106.72) * mm, "end": v(34.93, -114.3) * mm, "construction": true});
            skLineSegment(sketch, "E209.bottom", {"start": v(38.93, -106.54) * mm, "end": v(32.2, -99.8) * mm});
            skLineSegment(sketch, "E209.top", {"start": v(36.69, -108.78) * mm, "end": v(29.95, -102.05) * mm});
            skLineSegment(sketch, "E209.left", {"start": v(38.93, -106.54) * mm, "end": v(36.69, -108.78) * mm});
            skLineSegment(sketch, "E209.right", {"start": v(32.2, -99.8) * mm, "end": v(29.95, -102.05) * mm});
            skLineSegment(sketch, "E210", {"start": v(31.07, -100.92) * mm, "end": v(44.45, -114.3) * mm, "construction": true});
            skSolve(sketch);
        }
        {
            var Q0;
            Q0 = qSketchRegion(id + "F18", true);
            extrude(context, id + "F19", {"entities" : qUnion([Q0]), "operationType" : NewBodyOperationType.ADD, "depth" : 13.33 * mm, "offsetDistance" : 25.4 * mm});
        }
        {
            var Q0;
            Q0=makeQuery(id+"F19.opExtrude","SWEPT_FACE",FACE,{"disambiguationData":[OSD([sQuery(id+"F18.wireOp",EDGE,"E200.top")])]});
            var sketch = newSketch(context, id + "F20", { "sketchPlane" : qUnion([Q0])});
            skLineSegment(sketch, "E211.0", {"start": v(-93.34, 51.44) * mm, "end": v(-93.34, 38.1) * mm});
            skLineSegment(sketch, "E212.0", {"start": v(-102.86, 51.43) * mm, "end": v(-93.34, 51.43) * mm});
            skLineSegment(sketch, "E213", {"start": v(-93.34, 38.1) * mm, "end": v(-102.86, 51.44) * mm});
            skSolve(sketch);
        }
        {
            var Q0;
            Q0 = qSketchRegion(id + "F20", true);
            extrude(context, id + "F21", {"entities" : qUnion([Q0]), "operationType" : NewBodyOperationType.REMOVE, "endBound" : BoundingType.UP_TO_NEXT, "oppositeDirection" : true, "depth" : 25.4 * mm, "offsetDistance" : 25.4 * mm});
        }
        {
            var Q0;
            Q0=makeQuery(id+"F19.opExtrude","SWEPT_FACE",FACE,{"disambiguationData":[OSD([sQuery(id+"F18.wireOp",EDGE,"E203.bottom")])]});
            var sketch = newSketch(context, id + "F22", { "sketchPlane" : qUnion([Q0])});
            skLineSegment(sketch, "E214.0", {"start": v(-125.63, 51.44) * mm, "end": v(-116.1, 51.44) * mm});
            skLineSegment(sketch, "E215.0", {"start": v(-125.63, 51.44) * mm, "end": v(-125.63, 38.1) * mm});
            skLineSegment(sketch, "E216", {"start": v(-116.1, 51.44) * mm, "end": v(-125.63, 38.1) * mm});
            skSolve(sketch);
        }
        {
            var Q0;
            Q0 = qSketchRegion(id + "F22", true);
            extrude(context, id + "F23", {"entities" : qUnion([Q0]), "operationType" : NewBodyOperationType.REMOVE, "endBound" : BoundingType.UP_TO_NEXT, "oppositeDirection" : true, "depth" : 25.4 * mm, "offsetDistance" : 25.4 * mm});
        }
        {
            var Q0;
            Q0=makeQuery(id+"F19.opExtrude","SWEPT_FACE",FACE,{"disambiguationData":[OSD([sQuery(id+"F18.wireOp",EDGE,"E206.bottom")])]});
            var sketch = newSketch(context, id + "F24", { "sketchPlane" : qUnion([Q0])});
            skLineSegment(sketch, "E217.0", {"start": v(-116.1, 51.44) * mm, "end": v(-125.63, 51.44) * mm});
            skLineSegment(sketch, "E218.0", {"start": v(-125.63, 51.44) * mm, "end": v(-125.63, 38.1) * mm});
            skLineSegment(sketch, "E219", {"start": v(-116.1, 51.44) * mm, "end": v(-125.63, 38.1) * mm});
            skSolve(sketch);
        }
        {
            var Q0;
            Q0 = qSketchRegion(id + "F24", true);
            extrude(context, id + "F25", {"entities" : qUnion([Q0]), "operationType" : NewBodyOperationType.REMOVE, "endBound" : BoundingType.UP_TO_NEXT, "oppositeDirection" : true, "depth" : 25.4 * mm, "offsetDistance" : 25.4 * mm});
        }
        {
            var Q0;
            Q0=makeQuery(id+"F19.opExtrude","SWEPT_FACE",FACE,{"disambiguationData":[OSD([sQuery(id+"F18.wireOp",EDGE,"E194.top")])]});
            var sketch = newSketch(context, id + "F26", { "sketchPlane" : qUnion([Q0])});
            skLineSegment(sketch, "E220.0", {"start": v(-24.5, 51.44) * mm, "end": v(-34.03, 51.44) * mm});
            skLineSegment(sketch, "E221.0", {"start": v(-34.03, 51.44) * mm, "end": v(-34.03, 38.1) * mm});
            skLineSegment(sketch, "E222", {"start": v(-34.03, 38.1) * mm, "end": v(-24.5, 51.44) * mm});
            skSolve(sketch);
        }
        {
            var Q0;
            Q0 = qSketchRegion(id + "F26", true);
            extrude(context, id + "F27", {"entities" : qUnion([Q0]), "operationType" : NewBodyOperationType.REMOVE, "endBound" : BoundingType.UP_TO_NEXT, "oppositeDirection" : true, "depth" : 25.4 * mm, "offsetDistance" : 25.4 * mm});
        }
        {
            var Q0;
            Q0=makeQuery(id+"F19.opExtrude","SWEPT_FACE",FACE,{"disambiguationData":[OSD([sQuery(id+"F18.wireOp",EDGE,"E197.top")])]});
            var sketch = newSketch(context, id + "F28", { "sketchPlane" : qUnion([Q0])});
            skLineSegment(sketch, "E223.0", {"start": v(-44.55, 51.44) * mm, "end": v(-44.55, 38.1) * mm});
            skLineSegment(sketch, "E224.0", {"start": v(-54.07, 51.43) * mm, "end": v(-44.55, 51.43) * mm});
            skLineSegment(sketch, "E225", {"start": v(-54.07, 51.44) * mm, "end": v(-44.55, 38.1) * mm});
            skSolve(sketch);
        }
        {
            var Q0;
            Q0 = qSketchRegion(id + "F28", true);
            extrude(context, id + "F29", {"entities" : qUnion([Q0]), "operationType" : NewBodyOperationType.REMOVE, "endBound" : BoundingType.UP_TO_NEXT, "oppositeDirection" : true, "depth" : 25.4 * mm, "offsetDistance" : 25.4 * mm});
        }
        {
            var Q0;
            Q0=makeQuery(id+"F19.opExtrude","SWEPT_FACE",FACE,{"disambiguationData":[OSD([sQuery(id+"F18.wireOp",EDGE,"E187.bottom")])]});
            var sketch = newSketch(context, id + "F30", { "sketchPlane" : qUnion([Q0])});
            skLineSegment(sketch, "E226.0", {"start": v(-44.55, 51.44) * mm, "end": v(-44.55, 38.1) * mm});
            skLineSegment(sketch, "E227.0", {"start": v(-44.55, 51.44) * mm, "end": v(-54.07, 51.44) * mm});
            skLineSegment(sketch, "E228", {"start": v(-54.07, 51.44) * mm, "end": v(-44.55, 38.1) * mm});
            skSolve(sketch);
        }
        {
            var Q0;
            Q0 = qSketchRegion(id + "F30", true);
            extrude(context, id + "F31", {"entities" : qUnion([Q0]), "operationType" : NewBodyOperationType.REMOVE, "endBound" : BoundingType.UP_TO_NEXT, "oppositeDirection" : true, "depth" : 25.4 * mm, "offsetDistance" : 25.4 * mm});
        }
        {
            var Q0;
            Q0=makeQuery(id+"F19.opExtrude","SWEPT_FACE",FACE,{"disambiguationData":[OSD([sQuery(id+"F18.wireOp",EDGE,"E190.bottom")])]});
            var sketch = newSketch(context, id + "F32", { "sketchPlane" : qUnion([Q0])});
            skLineSegment(sketch, "E229.0", {"start": v(-24.48, 51.43) * mm, "end": v(-34, 51.43) * mm});
            skLineSegment(sketch, "E230.0", {"start": v(-34, 51.44) * mm, "end": v(-34, 38.1) * mm});
            skLineSegment(sketch, "E231", {"start": v(-24.48, 51.44) * mm, "end": v(-34, 38.1) * mm});
            skSolve(sketch);
        }
        {
            var Q0;
            Q0 = qSketchRegion(id + "F32", true);
            extrude(context, id + "F33", {"entities" : qUnion([Q0]), "operationType" : NewBodyOperationType.REMOVE, "endBound" : BoundingType.UP_TO_NEXT, "oppositeDirection" : true, "depth" : 25.4 * mm, "offsetDistance" : 25.4 * mm});
        }
    });
